# Revit family: LAMP_FIL 45 840MM OPAL COMFORT RECESSED
name_source: partatom
category: Luminarias
revit_build: Autodesk Revit 2018 (Build: 20170223_1515(x64)
units: mm (PartAtom-declared; Revit-internal decimal feet)

## family parameters
Anfitrión = Cara
Compartido = No
Corte con vacíos al cargar = No
Cota de conector redondo = Diámetro de uso
Origen de luz = Sí
Punto de cálculo de habitación = No
Tipo de pieza = Normal

## types (12) — shared parameters
CRI = 80
Cambio de temperatura de color de luz atenuada = <Ninguno>
Dimensions = 840x55x76
Elevación por defecto = 1219 mm
Fabricante = LAMP
Filtro de color = 16777215
Gear = Electronic
IEE = A+
Installation instructions = https://www.lamp.es
Insulation class = I
LED Lifetime = 70.000 L80 B10
Lamp = MID-POWER LED
Last update = 30/03/2021
Longitud de línea de emisión = 840 mm  [stored 2.75591 ft]
MacAdam = 3
Manufacturer URL = http://www.lamp.es
Manufacturer country = Spain
Manufacturer name = LAMP
Material difusor = LAMP_PC Difusor Opal Fil
Material suspension = LAMP_Acero genérico
Plum = 13 W
Power = 12 W
Power Supply = 220-240V 50/60Hz
Product URL = https://www.lamp.es
Product datasheet = http://www.lamp.es
Protection rating = IP20 / IK07
Recessed dimensions = 846x51x0
Type = MID POWER TRIDONIC
Ángulo de inclinación = -90.00°

## per-type parameters (varying)
| type | Archivo de red fotométrica | Descripción | Efficacy | Finish | Material perfil | Modelo | Product code | Weight |
| 1950LM 3000K DALI BLACK | F41RE084MOPR830nB.IES | FIL45 REC 840 1950 WW OP COMF DALI BK. | 94 lm/W | Matte black RAL 9011 | LAMP_Aluminio Perfil Fil NG | F41RE084MOPR830DB | F41RE084MOPR830DB | 2.17 kg |
| 1950LM 3000K DALI GREY | F41RE084MOPR830nG.IES | FIL45 REC 840 1950 WW OP COMF DALI GR. | 94 lm/W | Gloss grey | LAMP_Aluminio Perfil Fil GR | F41RE084MOPR830DG | F41RE084MOPR830DG | 2.17 kg |
| 1950LM 3000K DALI WHITE | F41RE084MOPR830nW.IES | FIL45 REC 840 1950 WW OP COMF DALI WH. | 94 lm/W | Matte white RAL 9010 | LAMP_Aluminio Perfil Fil BL | F41RE084MOPR830DW | F41RE084MOPR830DW | 2.17 kg |
| 1950LM 3000K  BLACK | F41RE084MOPR830NB.IES | FIL45 REC 840 1950 WW OP COMF BK. | 94 lm/W | Matte black RAL 9011 | LAMP_Aluminio Perfil Fil NG | F41RE084MOPR830NB | F41RE084MOPR830NB | 2.04 kg |
| 1950LM 3000K  GREY | F41RE084MOPR830NG.IES | FIL45 REC 840 1950 WW OP COMF GR. | 94 lm/W | Gloss grey | LAMP_Aluminio Perfil Fil GR | F41RE084MOPR830NG | F41RE084MOPR830NG | 2.04 kg |
| 1950LM 3000K  WHITE | F41RE084MOPR830NW.IES | FIL45 REC 840 1950 WW OP COMF WH. | 94 lm/W | Matte white RAL 9010 | LAMP_Aluminio Perfil Fil BL | F41RE084MOPR830NW | F41RE084MOPR830NW | 2.04 kg |
| 1950LM 4000K DALI BLACK | F41RE084MOPR840nB.IES | FIL45 REC 840 1950 NW OP COMF DALI BK. | 99 lm/W | Matte black RAL 9011 | LAMP_Aluminio Perfil Fil NG | F41RE084MOPR840DB | F41RE084MOPR840DB | 2.17 kg |
| 1950LM 4000K DALI GREY | F41RE084MOPR840nG.IES | FIL45 REC 840 1950 NW OP COMF DALI GR. | 99 lm/W | Gloss grey | LAMP_Aluminio Perfil Fil GR | F41RE084MOPR840DG | F41RE084MOPR840DG | 2.17 kg |
| 1950LM 4000K DALI WHITE | F41RE084MOPR840nW.IES | FIL45 REC 840 1950 NW OP COMF DALI WH. | 99 lm/W | Matte white RAL 9010 | LAMP_Aluminio Perfil Fil BL | F41RE084MOPR840DW | F41RE084MOPR840DW | 2.17 kg |
| 1950LM 4000K  BLACK | F41RE084MOPR840NB.IES | FIL45 REC 840 1950 NW OP COMF BK. | 99 lm/W | Matte black RAL 9011 | LAMP_Aluminio Perfil Fil NG | F41RE084MOPR840NB | F41RE084MOPR840NB | 2.04 kg |
| 1950LM 4000K  GREY | F41RE084MOPR840NG.IES | FIL45 REC 840 1950 NW OP COMF GR. | 99 lm/W | Gloss grey | LAMP_Aluminio Perfil Fil GR | F41RE084MOPR840NG | F41RE084MOPR840NG | 2.04 kg |
| 1950LM 4000K  WHITE | F41RE084MOPR840NW.IES | FIL45 REC 840 1950 NW OP COMF WH. | 99 lm/W | Matte white RAL 9010 | LAMP_Aluminio Perfil Fil BL | F41RE084MOPR840NW | F41RE084MOPR840NW | 2.04 kg |

note: [stored X ft] marks values corroborated as IEEE doubles in the binary element streams (Revit-internal decimal feet)
